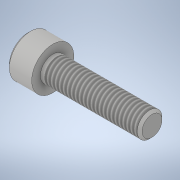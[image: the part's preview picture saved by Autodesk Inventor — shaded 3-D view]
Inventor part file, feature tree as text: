
AUTODESK INVENTOR PART (.ipt)
format: ipt  version: 2022 (Build 260153000, 153)  size: 153,600 bytes
history: native  units: mm
features: other x14, sketch x3, revolve x1, thread x1, hole x1, extrude x1
ambient origin geometry x8: Origin, YZ Plane, XZ Plane, XY Plane, X Axis, Y Axis, Z Axis, Center Point
bodies: Solid1 (feature_tree)
feature tree (21):
  revolve  "Revolution1"  [1 undecoded]
  thread  "Thread1"  [1 undecoded]
  hole  "Hole1"  [1 undecoded]
  extrude  "Extrusion1"  [1 undecoded]
  other  "bolt_XY"
  other  "bolt_YZ"
  other  "bolt_ZX"
  other  "bolt_X"
  other  "bolt_Y"
  other  "bolt_Z"
  other  "bolt_Center"
  other  "nut_XY"
  other  "nut_YZ"
  other  "nut_ZX"
  other  "nut_X"
  other  "nut_Y"
  other  "nut_Z"
  other  "nut_Center"
  sketch  "Sketch_1"  dims[d0=360.0deg d1=19.2mm d2=0.8mm]
  sketch  "Sketch2"  dims[d3=4.0mm d4=6.0mm d5=4.0mm d6=2.0mm d7=90.0deg d8=2.5mm d9=120.0deg d10=2.5mm d11=0.0mm]
  sketch  "Sketch_3"  dims[d12=0.0mm d13=0.0mm]
note: 4 required parameter values undecoded (feature->parameter linkage not recoverable at this tier; creation-order binding heuristic only, values carry confidence <= 0.55)